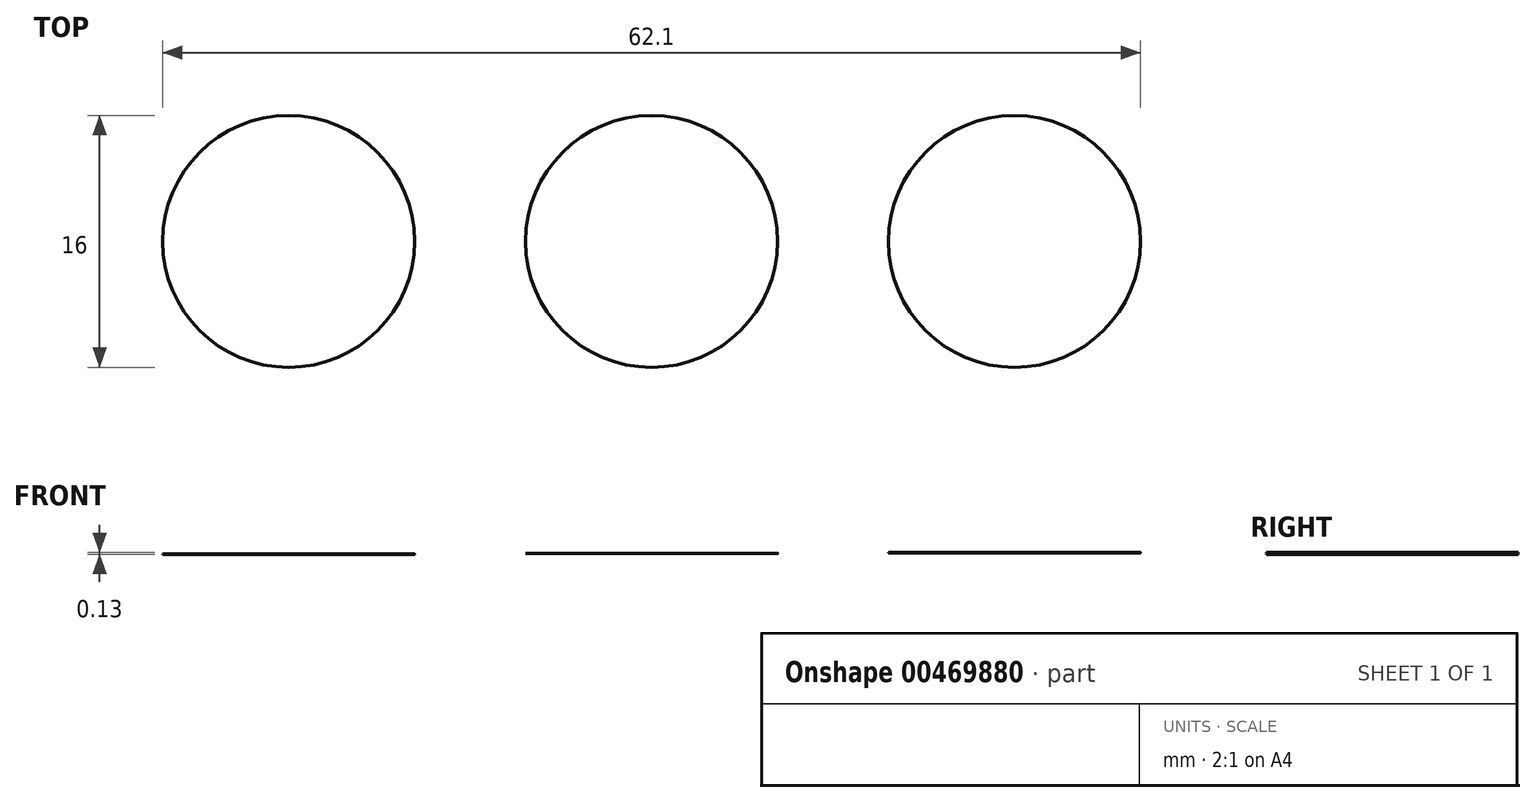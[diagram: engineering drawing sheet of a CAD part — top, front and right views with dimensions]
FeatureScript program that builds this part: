
annotation { "Feature Type Name" : "Feature", "Feature Type Description" : "" }
export const myFeature = defineFeature(function(context is Context, id is Id, definition is map)
    precondition{}
    {
        {
            var Q0;
            Q0=qCreatedBy(makeId("Top.planeOp"),FACE);
            var sketch = newSketch(context, id + "F0", { "sketchPlane" : qUnion([Q0])});
            skPoint(sketch, "E0.middle", {"position": v(0, 0) * mm});
            skCircle(sketch, "E1", {"center": v(0, 0) * mm, "radius": 8 * mm});
            skPoint(sketch, "E2", {"position": v(23.05, 0) * mm});
            skPoint(sketch, "E3", {"position": v(-23.05, 0) * mm});
            skCircle(sketch, "E4", {"center": v(23.05, 0) * mm, "radius": 8 * mm});
            skCircle(sketch, "E5", {"center": v(-23.05, 0) * mm, "radius": 8 * mm});
            skPoint(sketch, "E6.start.orphan", {"position": v(-8, 0) * mm});
            skPoint(sketch, "E7.orphan", {"position": v(8, 0) * mm});
            skSolve(sketch);
        }
        {
            var Q0;
            Q0=makeQuery(id+"F0.imprint","IMPRINT",FACE,{"disambiguationData":[TD([[makeQuery(id+"F0.imprint","IMPRINT",EDGE,{"derivedFrom":sQuery(id+"F0.wireOp",EDGE,"E5")}),1.0]])]});
            var Q1;
            Q1=makeQuery(id+"F0.imprint","IMPRINT",FACE,{"disambiguationData":[TD([[makeQuery(id+"F0.imprint","IMPRINT",EDGE,{"derivedFrom":sQuery(id+"F0.wireOp",EDGE,"E1")}),1.0]])]});
            var Q2;
            Q2=makeQuery(id+"F0.imprint","IMPRINT",FACE,{"disambiguationData":[TD([[makeQuery(id+"F0.imprint","IMPRINT",EDGE,{"derivedFrom":sQuery(id+"F0.wireOp",EDGE,"E4")}),1.0]])]});
            extrude(context, id + "F1", {"entities" : qUnion([Q0, Q1, Q2]), "depth" : 0.03 * mm});
        }
        {
            var Q0;
            Q0=makeQuery(id+"F1.opExtrude","SWEPT_BODY",BODY,{"disambiguationData":[OSD([sQuery(id+"F0.wireOp",EDGE,"E1")])]});
            var Q1;
            Q1=qCreatedBy(makeId("Top.planeOp"),FACE);
            transform(context, id + "F2", {"entities" : qUnion([Q0]), "transformType" : TransformType.TRANSLATION_DISTANCE, "transformDirection" : qUnion([Q1]), "distance" : 0.05 * mm, "makeCopy" : false});
        }
        {
            var Q0;
            Q0=makeQuery(id+"F1.opExtrude","SWEPT_BODY",BODY,{"disambiguationData":[OSD([sQuery(id+"F0.wireOp",EDGE,"E4")])]});
            var Q1;
            Q1=qCreatedBy(makeId("Top.planeOp"),FACE);
            transform(context, id + "F3", {"entities" : qUnion([Q0]), "transformType" : TransformType.TRANSLATION_DISTANCE, "transformDirection" : qUnion([Q1]), "distance" : 0.1 * mm, "makeCopy" : false});
        }
    });
